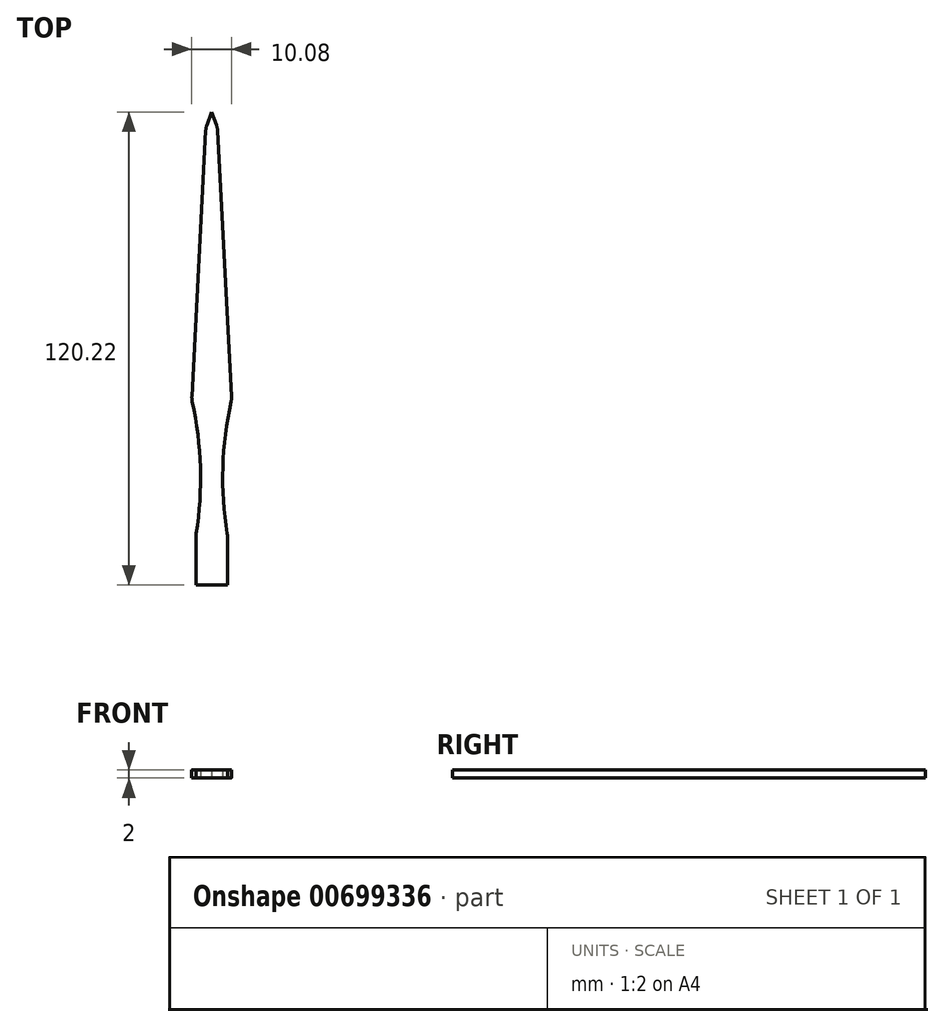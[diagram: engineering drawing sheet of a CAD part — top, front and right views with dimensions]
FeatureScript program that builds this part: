
annotation { "Feature Type Name" : "Feature", "Feature Type Description" : "" }
export const myFeature = defineFeature(function(context is Context, id is Id, definition is map)
    precondition{}
    {
        {
            var Q0;
            Q0=qCreatedBy(makeId("Top.planeOp"),FACE);
            var sketch = newSketch(context, id + "F0", { "sketchPlane" : qUnion([Q0])});
            skLineSegment(sketch, "E0.bottom", {"start": v(-4, 0) * mm, "end": v(0, 0) * mm});
            skLineSegment(sketch, "E1", {"start": v(-5.07, 47.28) * mm, "end": v(-1.46, 116.21) * mm});
            skLineSegment(sketch, "E2", {"start": v(-1.46, 116.21) * mm, "end": v(0, 120.22) * mm});
            skPoint(sketch, "E3.orphan", {"position": v(0, 144.08) * mm});
            skArc(sketch, "E4", {"start": v(-4, 12.71) * mm, "mid": v(-2.86, 30.05) * mm, "end": v(-5.07, 47.28) * mm});
            skLineSegment(sketch, "E5", {"start": v(-4, 0) * mm, "end": v(-4, 12.71) * mm});
            skLineSegment(sketch, "E6", {"start": v(0, -82.01) * mm, "end": v(0, 148.8) * mm, "construction": true});
            skLineSegment(sketch, "E7.MirrorCS", {"start": v(5.07, 47.28) * mm, "end": v(1.46, 116.21) * mm});
            skArc(sketch, "E8.MirrorCS", {"start": v(4, 12.71) * mm, "mid": v(2.86, 30.05) * mm, "end": v(5.07, 47.28) * mm});
            skLineSegment(sketch, "E9.MirrorCS", {"start": v(4, 0) * mm, "end": v(4, 12.71) * mm});
            skLineSegment(sketch, "E10.MirrorCS", {"start": v(4, 0) * mm, "end": v(0, 0) * mm});
            skLineSegment(sketch, "E11.MirrorCS", {"start": v(1.46, 116.21) * mm, "end": v(0, 120.22) * mm});
            skSolve(sketch);
        }
        {
            var Q0;
            Q0=makeQuery(id+"F0.imprint","IMPRINT",FACE,{"disambiguationData":[TD([[makeQuery(id+"F0.imprint","IMPRINT",EDGE,{"derivedFrom":sQuery(id+"F0.wireOp",EDGE,"E0.bottom")}),1.0]])]});
            extrude(context, id + "F1", {"entities" : qUnion([Q0]), "depth" : 2 * mm, "offsetDistance" : 25 * mm});
        }
        {
            var Q0;
            Q0=makeQuery(id+"F1.opExtrude","SWEPT_EDGE",EDGE,{"disambiguationData":[OSD([sQuery(id+"F0.wireOp",EDGE,"E1"),sQuery(id+"F0.wireOp",EDGE,"E2")])]});
            var Q1;
            Q1=makeQuery(id+"F1.opExtrude","SWEPT_EDGE",EDGE,{"disambiguationData":[OSD([sQuery(id+"F0.wireOp",EDGE,"E7.MirrorCS"),sQuery(id+"F0.wireOp",EDGE,"E11.MirrorCS")])]});
            var Q2;
            Q2=makeQuery(id+"F1.opExtrude","SWEPT_EDGE",EDGE,{"disambiguationData":[OSD([sQuery(id+"F0.wireOp",EDGE,"E7.MirrorCS"),sQuery(id+"F0.wireOp",EDGE,"E8.MirrorCS")])]});
            var Q3;
            Q3=makeQuery(id+"F1.opExtrude","SWEPT_EDGE",EDGE,{"disambiguationData":[OSD([sQuery(id+"F0.wireOp",EDGE,"E1"),sQuery(id+"F0.wireOp",EDGE,"E4")])]});
            var Q4;
            Q4=makeQuery(id+"F1.opExtrude","SWEPT_EDGE",EDGE,{"disambiguationData":[OSD([sQuery(id+"F0.wireOp",EDGE,"E4"),sQuery(id+"F0.wireOp",EDGE,"E5")])]});
            var Q5;
            Q5=makeQuery(id+"F1.opExtrude","SWEPT_EDGE",EDGE,{"disambiguationData":[OSD([sQuery(id+"F0.wireOp",EDGE,"E8.MirrorCS"),sQuery(id+"F0.wireOp",EDGE,"E9.MirrorCS")])]});
            fillet(context, id + "F2", {"entities" : qUnion([Q0, Q1, Q2, Q3, Q4, Q5]), "radius" : 5 * mm, "tangentPropagation" : true, "allowEdgeOverflow" : false});
        }
    });
